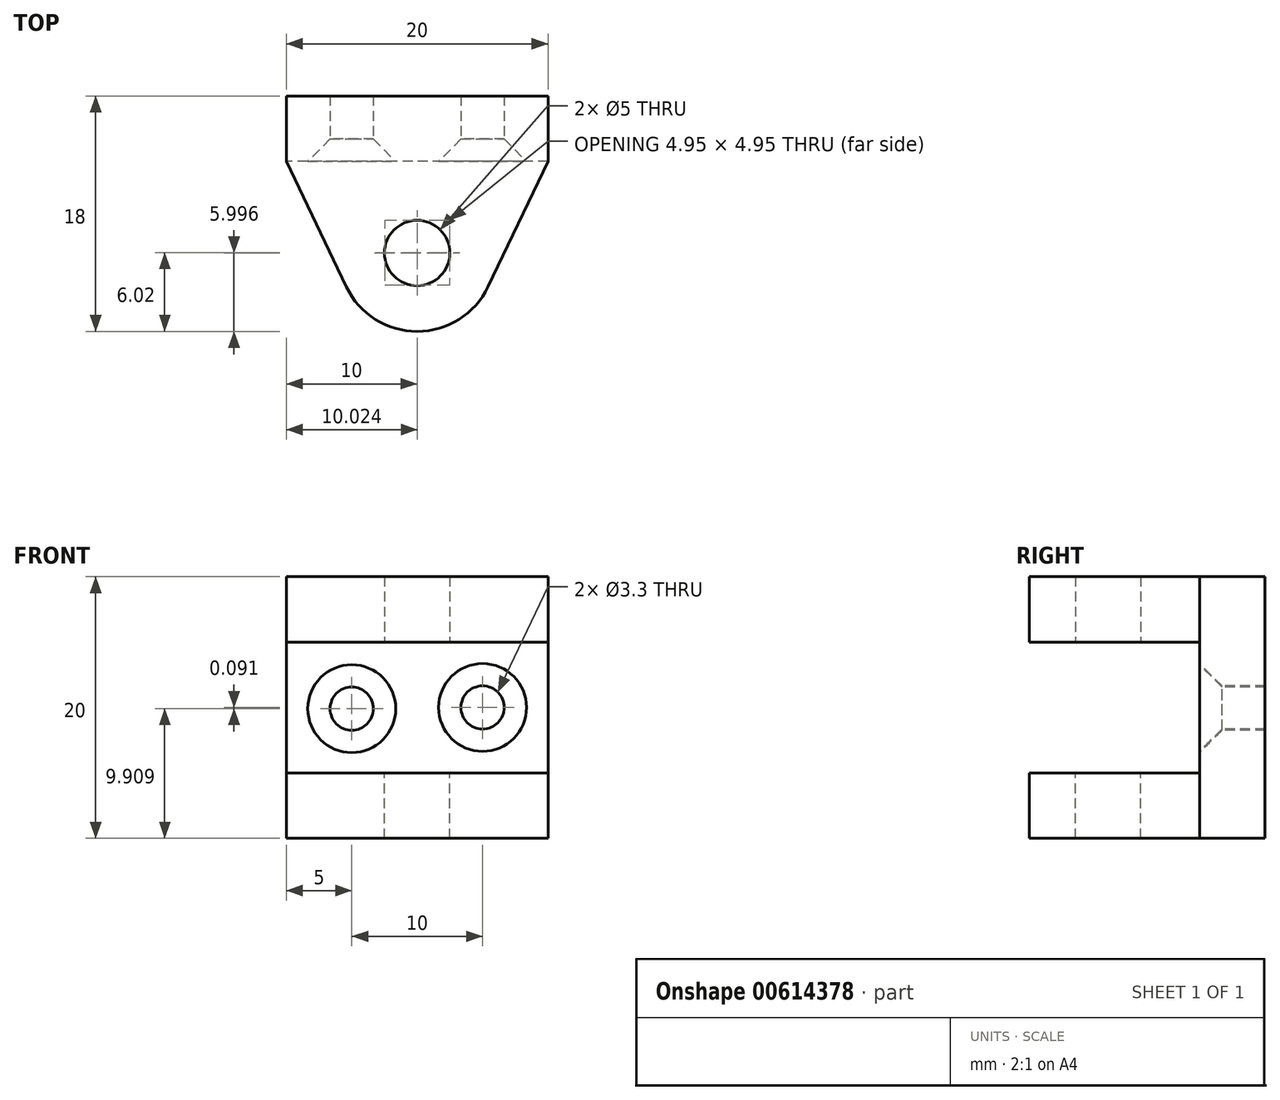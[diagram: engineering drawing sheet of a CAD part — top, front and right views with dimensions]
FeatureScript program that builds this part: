
annotation { "Feature Type Name" : "Feature", "Feature Type Description" : "" }
export const myFeature = defineFeature(function(context is Context, id is Id, definition is map)
    precondition{}
    {
        {
            var Q0;
            Q0=qCreatedBy(makeId("Right.planeOp"),FACE);
            var sketch = newSketch(context, id + "F0", { "sketchPlane" : qUnion([Q0])});
            skLineSegment(sketch, "E0", {"start": v(-2.35, 8.34) * mm, "end": v(-2.35, -11.66) * mm});
            skLineSegment(sketch, "E1", {"start": v(-2.35, -11.66) * mm, "end": v(-20.35, -11.66) * mm});
            skLineSegment(sketch, "E2", {"start": v(-20.35, -11.66) * mm, "end": v(-20.35, -6.66) * mm});
            skLineSegment(sketch, "E3", {"start": v(-20.35, -6.66) * mm, "end": v(-7.35, -6.66) * mm});
            skLineSegment(sketch, "E4", {"start": v(-7.35, -6.66) * mm, "end": v(-7.35, 3.34) * mm});
            skLineSegment(sketch, "E5", {"start": v(-7.35, 3.34) * mm, "end": v(-20.35, 3.34) * mm});
            skLineSegment(sketch, "E6", {"start": v(-20.35, 3.34) * mm, "end": v(-20.35, 8.34) * mm});
            skLineSegment(sketch, "E7", {"start": v(-20.35, 8.34) * mm, "end": v(-2.35, 8.34) * mm});
            skSolve(sketch);
        }
        {
            var Q0;
            Q0=makeQuery(id+"F0.imprint","IMPRINT",FACE,{"disambiguationData":[TD([[makeQuery(id+"F0.imprint","IMPRINT",EDGE,{"derivedFrom":sQuery(id+"F0.wireOp",EDGE,"E0")}),-1.0]])]});
            extrude(context, id + "F1", {"entities" : qUnion([Q0]), "depth" : 20 * mm, "offsetDistance" : 25 * mm});
        }
        {
            var Q0;
            Q0=makeQuery(id+"F1.opExtrude","SWEPT_FACE",FACE,{"disambiguationData":[OSD([sQuery(id+"F0.wireOp",EDGE,"E3")])]});
            var sketch = newSketch(context, id + "F2", { "sketchPlane" : qUnion([Q0])});
            skCircle(sketch, "E8", {"center": v(10, -14.35) * mm, "radius": 2.5 * mm});
            skPoint(sketch, "E8.centerSnap0", {"position": v(10, -20.35) * mm});
            skArc(sketch, "E9", {"start": v(4.59, -16.94) * mm, "mid": v(10, -20.35) * mm, "end": v(15.41, -16.94) * mm});
            skLineSegment(sketch, "E10", {"start": v(20, -7.35) * mm, "end": v(15.41, -16.94) * mm});
            skLineSegment(sketch, "E11", {"start": v(0, -7.35) * mm, "end": v(4.59, -16.94) * mm});
            skSolve(sketch);
        }
        {
            var Q0;
            {var subQ0=sQuery(id+"F2.wireOp",EDGE,"E11");Q0=makeQuery(id+"F2.imprint","IMPRINT",FACE,{"disambiguationData":[TD([[makeQuery(id+"F2.imprint","IMPRINT",EDGE,{"derivedFrom":subQ0}),-1.0]])]});}
            var Q1;
            {var subQ0=sQuery(id+"F2.wireOp",EDGE,"E10");Q1=makeQuery(id+"F2.imprint","IMPRINT",FACE,{"disambiguationData":[TD([[makeQuery(id+"F2.imprint","IMPRINT",EDGE,{"derivedFrom":subQ0}),1.0]])]});}
            extrude(context, id + "F3", {"entities" : qUnion([Q0, Q1]), "operationType" : NewBodyOperationType.REMOVE, "endBound" : BoundingType.SYMMETRIC, "depth" : 34.8 * mm, "offsetDistance" : 25 * mm});
        }
        {
            var Q0;
            Q0=sQuery(id+"F2.wireOp",VERTEX,"E8.center");
            var Q1;
            Q1=makeQuery(id+"F1.opExtrude","SWEPT_BODY",BODY,{"disambiguationData":[OSD([sQuery(id+"F0.wireOp",EDGE,"E0"),sQuery(id+"F0.wireOp",EDGE,"E1"),sQuery(id+"F0.wireOp",EDGE,"E2"),sQuery(id+"F0.wireOp",EDGE,"E3"),sQuery(id+"F0.wireOp",EDGE,"E4"),sQuery(id+"F0.wireOp",EDGE,"E5"),sQuery(id+"F0.wireOp",EDGE,"E6"),sQuery(id+"F0.wireOp",EDGE,"E7")])]});
            hole(context, id + "F4", {"style" : HoleStyle.SIMPLE, "endStyle" : HoleEndStyle.THROUGH, "standardTappedOrClearance" : lookupTablePath({ "standard" : "ISO", "size" : "5", "type" : "Drilled" }), "standardBlindInLast" : lookupTablePath({ "standard" : "ISO", "size" : "5", "type" : "Drilled" }), "holeDiameter" : 5 * mm, "majorDiameter" : 5 * mm, "isTappedThrough" : true, "tappedDepth" : 12 * mm, "tapClearance" : 3, "locations" : qUnion([Q0]), "scope" : qUnion([Q1])});
        }
        {
            var Q0;
            Q0=sQuery(id+"F2.wireOp",VERTEX,"E8.center");
            var Q1;
            Q1=makeQuery(id+"F1.opExtrude","SWEPT_BODY",BODY,{"disambiguationData":[OSD([sQuery(id+"F0.wireOp",EDGE,"E0"),sQuery(id+"F0.wireOp",EDGE,"E1"),sQuery(id+"F0.wireOp",EDGE,"E2"),sQuery(id+"F0.wireOp",EDGE,"E3"),sQuery(id+"F0.wireOp",EDGE,"E4"),sQuery(id+"F0.wireOp",EDGE,"E5"),sQuery(id+"F0.wireOp",EDGE,"E6"),sQuery(id+"F0.wireOp",EDGE,"E7")])]});
            hole(context, id + "F5", {"style" : HoleStyle.SIMPLE, "endStyle" : HoleEndStyle.THROUGH, "oppositeDirection" : true, "standardTappedOrClearance" : lookupTablePath({ "standard" : "ISO", "size" : "5", "type" : "Drilled" }), "standardBlindInLast" : lookupTablePath({ "standard" : "ISO", "size" : "5", "type" : "Drilled" }), "holeDiameter" : 5 * mm, "majorDiameter" : 5 * mm, "isTappedThrough" : true, "tappedDepth" : 12 * mm, "tapClearance" : 3, "locations" : qUnion([Q0]), "scope" : qUnion([Q1])});
        }
        {
            var Q0;
            Q0=makeQuery(id+"F1.opExtrude","SWEPT_FACE",FACE,{"disambiguationData":[OSD([sQuery(id+"F0.wireOp",EDGE,"E4")])]});
            var sketch = newSketch(context, id + "F6", { "sketchPlane" : qUnion([Q0])});
            skPoint(sketch, "E12", {"position": v(15, -1.66) * mm});
            skPoint(sketch, "E12.positionSnap0", {"position": v(20, -1.66) * mm});
            skPoint(sketch, "E13", {"position": v(5, -1.75) * mm});
            skSolve(sketch);
        }
        {
            var Q0;
            Q0=sQuery(id+"F6.wireOp",VERTEX,"E13");
            var Q1;
            Q1=sQuery(id+"F6.wireOp",VERTEX,"E12");
            var Q2;
            Q2=makeQuery(id+"F1.opExtrude","SWEPT_BODY",BODY,{"disambiguationData":[OSD([sQuery(id+"F0.wireOp",EDGE,"E0"),sQuery(id+"F0.wireOp",EDGE,"E1"),sQuery(id+"F0.wireOp",EDGE,"E2"),sQuery(id+"F0.wireOp",EDGE,"E3"),sQuery(id+"F0.wireOp",EDGE,"E4"),sQuery(id+"F0.wireOp",EDGE,"E5"),sQuery(id+"F0.wireOp",EDGE,"E6"),sQuery(id+"F0.wireOp",EDGE,"E7")])]});
            hole(context, id + "F7", {"style" : HoleStyle.C_SINK, "endStyle" : HoleEndStyle.THROUGH, "standardTappedOrClearance" : lookupTablePath({ "standard" : "ISO", "fit" : "Normal", "size" : "M3", "type" : "Clearance" }), "standardBlindInLast" : lookupTablePath({ "fit" : "Standard", "standard" : "ISO", "size" : "M3", "type" : "Clearance" }), "holeDiameter" : 3.3 * mm, "cSinkDiameter" : 6.72 * mm, "cSinkAngle" : 90 * degree, "majorDiameter" : 5 * mm, "isTappedThrough" : true, "tappedDepth" : 12 * mm, "tapClearance" : 3, "locations" : qUnion([Q0, Q1]), "scope" : qUnion([Q2])});
        }
    });
